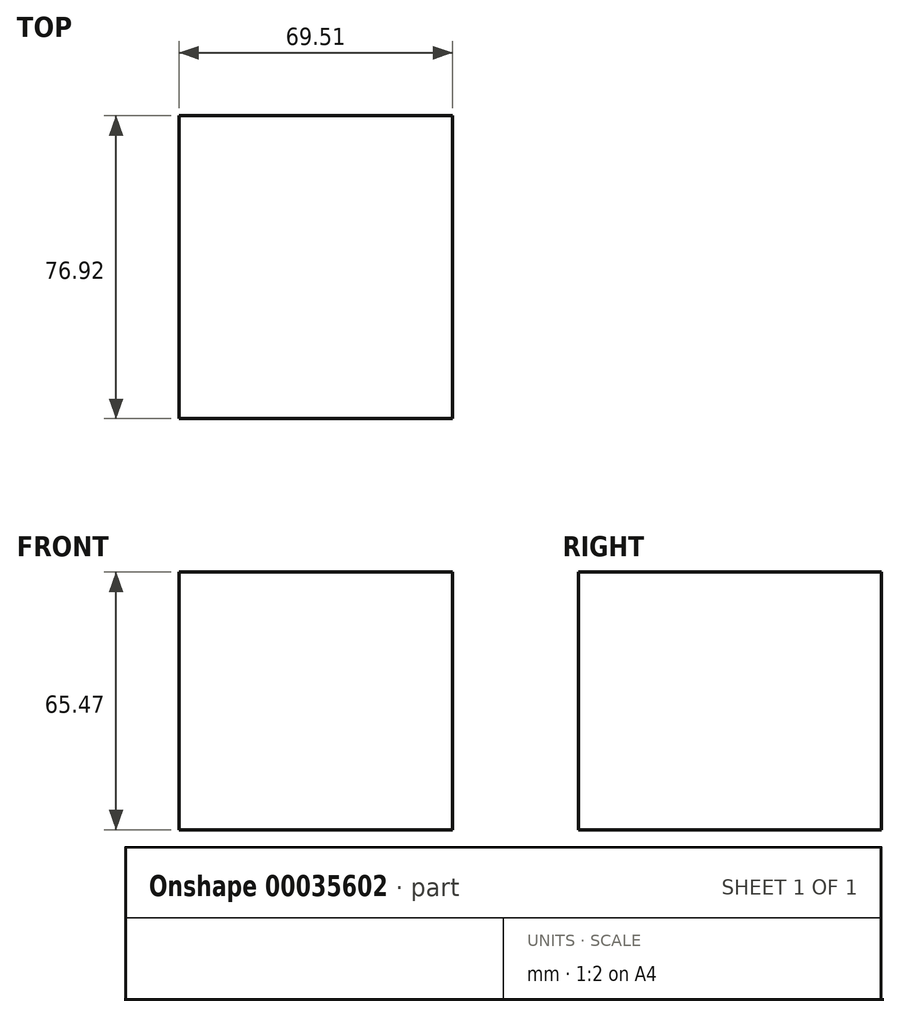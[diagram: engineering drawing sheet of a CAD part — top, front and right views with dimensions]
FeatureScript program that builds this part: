
annotation { "Feature Type Name" : "Feature", "Feature Type Description" : "" }
export const myFeature = defineFeature(function(context is Context, id is Id, definition is map)
    precondition{}
    {
        {
            var Q0;
            Q0=qCreatedBy(makeId("Front.planeOp"),FACE);
            var sketch = newSketch(context, id + "F0", { "sketchPlane" : qUnion([Q0])});
            skLineSegment(sketch, "E0.bottom", {"start": v(0, 0) * mm, "end": v(69.5, 0) * mm});
            skLineSegment(sketch, "E0.top", {"start": v(0, 65.47) * mm, "end": v(69.5, 65.47) * mm});
            skLineSegment(sketch, "E0.left", {"start": v(0, 0) * mm, "end": v(0, 65.47) * mm});
            skLineSegment(sketch, "E0.right", {"start": v(69.5, 0) * mm, "end": v(69.5, 65.47) * mm});
            skSolve(sketch);
        }
        {
            var Q0;
            Q0=makeQuery(id+"F0.imprint","IMPRINT",FACE,{"disambiguationData":[TD([[makeQuery(id+"F0.imprint","IMPRINT",EDGE,{"derivedFrom":sQuery(id+"F0.wireOp",EDGE,"E0.bottom")}),1.0]])]});
            extrude(context, id + "F1", {"entities" : qUnion([Q0]), "depth" : 76.92 * mm});
        }
    });
